# Revit family: Drinking_Fountain-Haws_Corporation-Wall_Mounted_1435 new
name_source: partatom
category: Plumbing Fixtures
revit_build: Autodesk Revit Architecture 2015 (Build: 20160512_1515(x64)
units: mm (PartAtom-declared; Revit-internal decimal feet)

## types (1)
- 1435
    Assembly Code = D2010810
    Bowl = Metal - Haws Corporation - White Enameled Iron
    CW Connection = Yes
    CWFU = 1
    Cost = 0 $
    Cost Note = For Cost information please visit the Resource tab in the Product Page URL
    Default Elevation = 3' - 0 5/8"
    Description = White enameled iron three bubbler drinking fountain with 100% lead-free waterways
    Flow = 0 GPM
    HW Connection = No
    HWFU = 0
    Keynote = 15410.A1
    Length = 4' - 11 1/4"
    Manufacturer = Haws Corporation
    Model = 1435
    Product Documentation Link = https://www.hawsco.com
    Product Page URL = https://www.hawsco.com
    Sanitary Radius = 0' - 0 3/4"
    Series = Three Bubbler Drinking Fountain
    Supply Radius = 0' - 0 1/4"
    Trap = Metal - Haws Corporation - High Polished Stainless Steel
    Tubing = Metal - Haws Corporation - Copper
    Type Comments = Gleaming white enameled iron construction
    URL = http://www.hawsco.com
    Vent Connection = No
    Version = 2014-v2.0a
    WFU = 1
    Waste Connection = Yes
    Waste Level = 2' - 11 1/2"

## geometry (parser evidence)
native form markers: Blend x36, Sweep x5
no freeform markers — native parametric forms only
